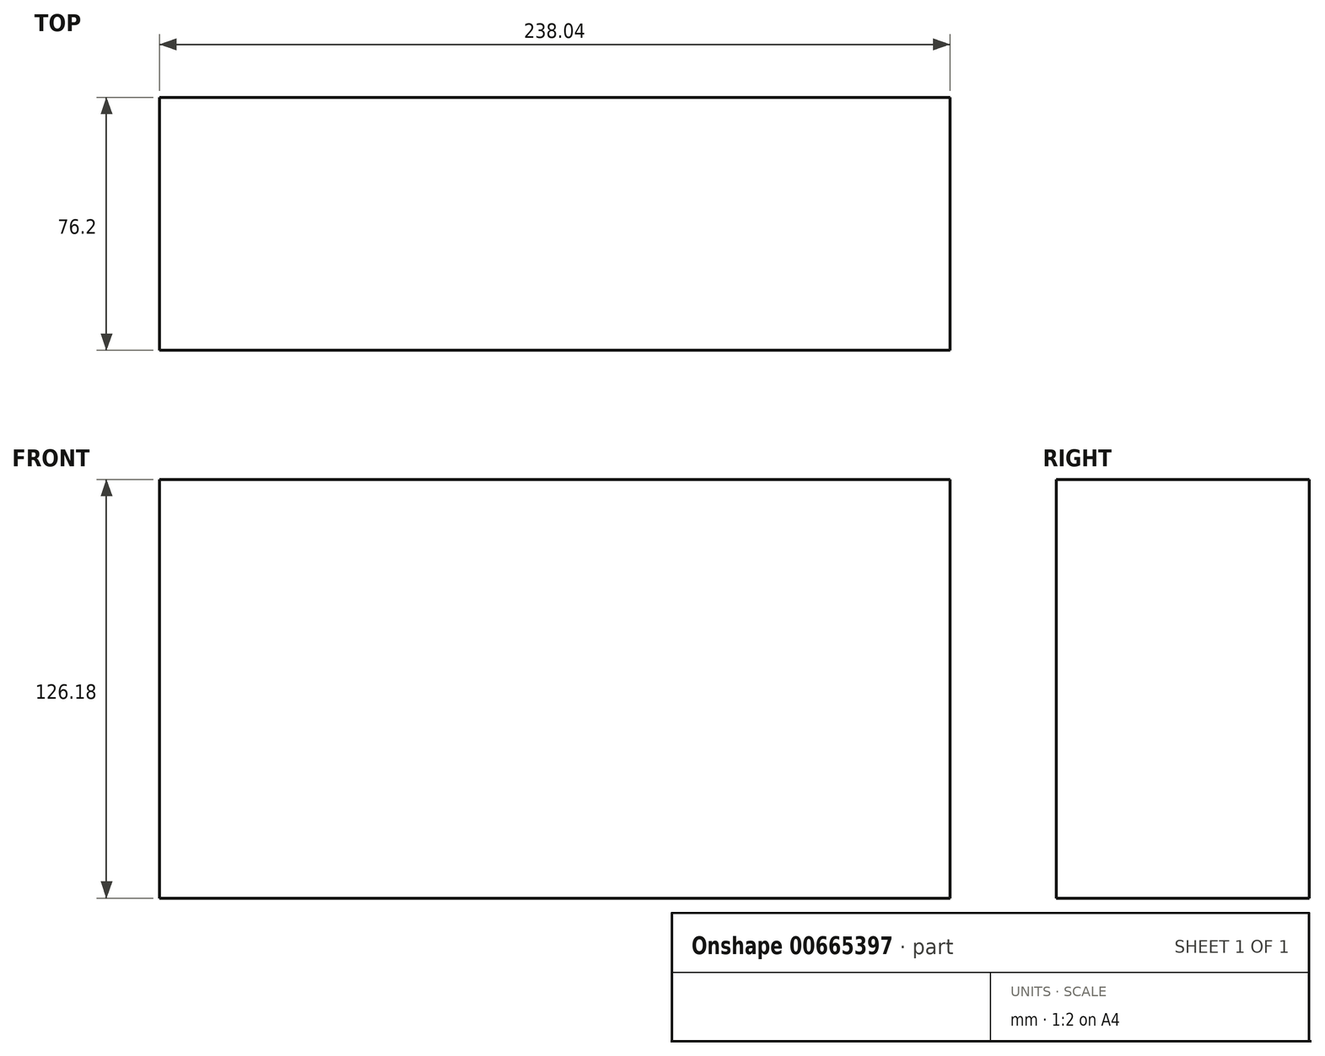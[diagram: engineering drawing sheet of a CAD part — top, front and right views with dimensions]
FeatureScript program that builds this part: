
annotation { "Feature Type Name" : "Feature", "Feature Type Description" : "" }
export const myFeature = defineFeature(function(context is Context, id is Id, definition is map)
    precondition{}
    {
        {
            var Q0;
            Q0=qCreatedBy(makeId("Front.planeOp"),FACE);
            var sketch = newSketch(context, id + "F0", { "sketchPlane" : qUnion([Q0])});
            skLineSegment(sketch, "E0.bottom", {"start": v(119.02, -63.1) * mm, "end": v(-119.02, -63.1) * mm});
            skLineSegment(sketch, "E0.top", {"start": v(119.02, 63.1) * mm, "end": v(-119.02, 63.1) * mm});
            skLineSegment(sketch, "E0.left", {"start": v(119.02, -63.1) * mm, "end": v(119.02, 63.1) * mm});
            skLineSegment(sketch, "E0.right", {"start": v(-119.02, -63.1) * mm, "end": v(-119.02, 63.1) * mm});
            skPoint(sketch, "E0.middle", {"position": v(0, 0) * mm});
            skSolve(sketch);
        }
        {
            var Q0;
            Q0 = qSketchRegion(id + "F0", true);
            extrude(context, id + "F1", {"entities" : qUnion([Q0]), "depth" : 76.2 * mm, "offsetDistance" : 25.4 * mm});
        }
    });
